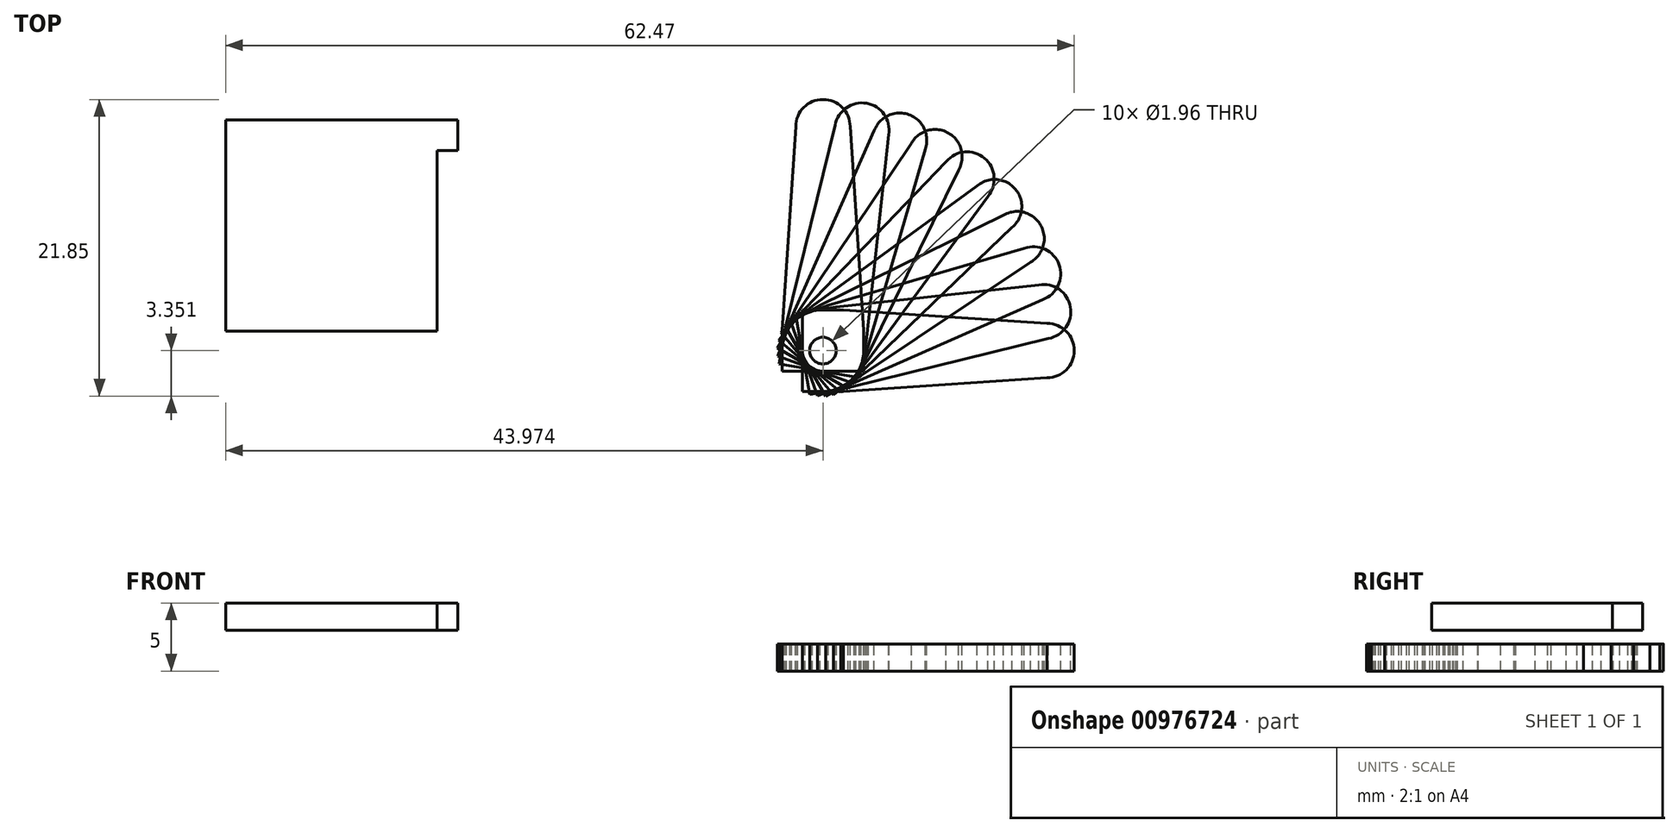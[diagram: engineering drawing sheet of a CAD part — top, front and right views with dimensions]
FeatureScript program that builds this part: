
annotation { "Feature Type Name" : "Feature", "Feature Type Description" : "" }
export const myFeature = defineFeature(function(context is Context, id is Id, definition is map)
    precondition{}
    {
        {
            var Q0;
            Q0=qCreatedBy(makeId("Top.planeOp"),FACE);
            var sketch = newSketch(context, id + "F0", { "sketchPlane" : qUnion([Q0])});
            skLineSegment(sketch, "E0.bottom", {"start": v(7.78, 7.78) * mm, "end": v(-7.78, 7.78) * mm});
            skLineSegment(sketch, "E0.top", {"start": v(7.78, -7.78) * mm, "end": v(-7.78, -7.78) * mm});
            skLineSegment(sketch, "E0.left", {"start": v(7.78, 7.78) * mm, "end": v(7.78, -7.78) * mm});
            skLineSegment(sketch, "E0.right", {"start": v(-7.78, 7.78) * mm, "end": v(-7.78, -7.78) * mm});
            skPoint(sketch, "E0.middle", {"position": v(0, 0) * mm});
            skLineSegment(sketch, "E1", {"start": v(7.78, 7.78) * mm, "end": v(9.3, 7.78) * mm});
            skLineSegment(sketch, "E2", {"start": v(9.3, 7.78) * mm, "end": v(9.3, 5.54) * mm});
            skLineSegment(sketch, "E3", {"start": v(9.3, 5.54) * mm, "end": v(7.78, 5.54) * mm});
            skLineSegment(sketch, "E4", {"start": v(8.54, 5.54) * mm, "end": v(8.54, 7.78) * mm, "construction": true});
            skCircle(sketch, "E5", {"center": v(8.54, 6.66) * mm, "radius": 0.5 * mm, "construction": true});
            skSolve(sketch);
        }
        {
            var Q0;
            Q0 = qSketchRegion(id + "F0", true);
            extrude(context, id + "F1", {"entities" : qUnion([Q0]), "depth" : 2 * mm, "offsetDistance" : 25 * mm});
        }
        {
            var Q0;
            Q0=makeQuery(id+"F1.opExtrude","CAP_FACE",FACE,{"disambiguationData":[OSD([sQuery(id+"F0.wireOp",EDGE,"E0.bottom"),sQuery(id+"F0.wireOp",EDGE,"E0.top"),sQuery(id+"F0.wireOp",EDGE,"E0.left"),sQuery(id+"F0.wireOp",EDGE,"E0.right"),sQuery(id+"F0.wireOp",EDGE,"E1"),sQuery(id+"F0.wireOp",EDGE,"E2"),sQuery(id+"F0.wireOp",EDGE,"E3")])],"isStart":true});
            cPlane(context, id + "F2", {"entities" : qUnion([Q0]), "cplaneType" : CPlaneType.OFFSET, "offset" : 1 * mm, "width" : 150 * mm, "height" : 150 * mm});
        }
        {
            var Q0;
            Q0=qCreatedBy(id+"F2.planeOp",FACE);
            var sketch = newSketch(context, id + "F3", { "sketchPlane" : qUnion([Q0])});
            skLineSegment(sketch, "E6", {"start": v(34.2, -7.3) * mm, "end": v(33.2, 7.7) * mm});
            skLineSegment(sketch, "E7", {"start": v(33.2, 7.7) * mm, "end": v(39.2, 7.7) * mm});
            skLineSegment(sketch, "E8", {"start": v(39.2, 7.7) * mm, "end": v(38.2, -7.3) * mm});
            skLineSegment(sketch, "E9", {"start": v(34.2, -7.3) * mm, "end": v(38.2, -7.3) * mm, "construction": true});
            skArc(sketch, "E10", {"start": v(34.2, -7.3) * mm, "mid": v(36.2, -9.3) * mm, "end": v(38.2, -7.3) * mm});
            skLineSegment(sketch, "E11", {"start": v(36.2, -7.3) * mm, "end": v(36.2, 7.7) * mm, "construction": true});
            skCircle(sketch, "E12", {"center": v(36.2, 9.2) * mm, "radius": 0.98 * mm});
            skLineSegment(sketch, "E13.top", {"start": v(33.2, 10.72) * mm, "end": v(39.2, 10.72) * mm});
            skLineSegment(sketch, "E13.left", {"start": v(33.2, 7.7) * mm, "end": v(33.2, 10.72) * mm});
            skLineSegment(sketch, "E13.right", {"start": v(39.2, 7.7) * mm, "end": v(39.2, 10.72) * mm});
            skSolve(sketch);
        }
        {
            var Q0;
            Q0 = qSketchRegion(id + "F3", true);
            extrude(context, id + "F4", {"entities" : qUnion([Q0]), "depth" : 2 * mm, "offsetDistance" : 25 * mm});
        }
        {
            var Q0;
            Q0=makeQuery(id+"F4.opExtrude","SWEPT_BODY",BODY,{"disambiguationData":[OSD([sQuery(id+"F3.wireOp",EDGE,"E6"),sQuery(id+"F3.wireOp",EDGE,"E8"),sQuery(id+"F3.wireOp",EDGE,"E10"),sQuery(id+"F3.wireOp",EDGE,"E12"),sQuery(id+"F3.wireOp",EDGE,"E13.top"),sQuery(id+"F3.wireOp",EDGE,"E13.left"),sQuery(id+"F3.wireOp",EDGE,"E13.right")])]});
            var Q1;
            Q1=makeQuery(id+"F4.opExtrude","SWEPT_FACE",FACE,{"disambiguationData":[OSD([sQuery(id+"F3.wireOp",EDGE,"E12")])]});
            circularPattern(context, id + "F5", {"entities" : qUnion([Q0]), "axis" : qUnion([Q1]), "angle" : 90 * degree, "instanceCount" : 10, "equalSpace" : true});
        }
    });
